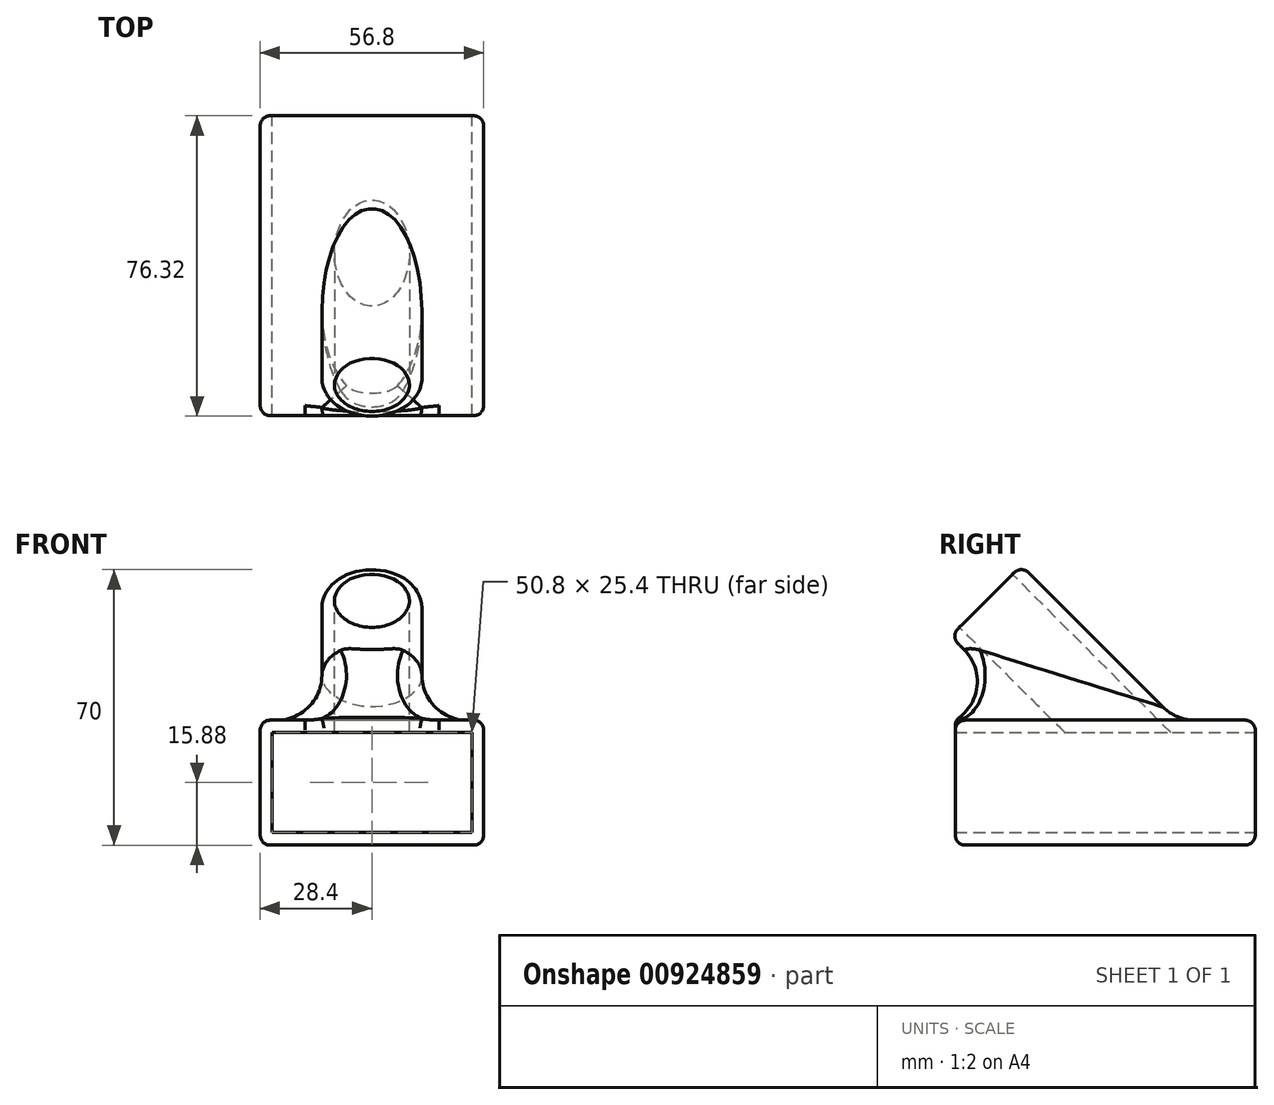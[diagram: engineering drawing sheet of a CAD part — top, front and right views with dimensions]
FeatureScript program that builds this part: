
annotation { "Feature Type Name" : "Feature", "Feature Type Description" : "" }
export const myFeature = defineFeature(function(context is Context, id is Id, definition is map)
    precondition{}
    {
        {
            var Q0;
            Q0=qCreatedBy(makeId("Front.planeOp"),FACE);
            var sketch = newSketch(context, id + "F0", { "sketchPlane" : qUnion([Q0])});
            skLineSegment(sketch, "E0.bottom", {"start": v(28.4, -15.88) * mm, "end": v(-28.4, -15.88) * mm});
            skLineSegment(sketch, "E0.top", {"start": v(28.4, 15.88) * mm, "end": v(-28.4, 15.87) * mm});
            skLineSegment(sketch, "E0.left", {"start": v(28.4, -15.88) * mm, "end": v(28.4, 15.88) * mm});
            skLineSegment(sketch, "E0.right", {"start": v(-28.4, -15.88) * mm, "end": v(-28.4, 15.88) * mm});
            skPoint(sketch, "E0.middle", {"position": v(0, 0) * mm});
            skLineSegment(sketch, "E1.bottom", {"start": v(25.4, -12.7) * mm, "end": v(-25.4, -12.7) * mm});
            skLineSegment(sketch, "E1.top", {"start": v(25.4, 12.7) * mm, "end": v(-25.4, 12.7) * mm});
            skLineSegment(sketch, "E1.left", {"start": v(25.4, -12.7) * mm, "end": v(25.4, 12.7) * mm});
            skLineSegment(sketch, "E1.right", {"start": v(-25.4, -12.7) * mm, "end": v(-25.4, 12.7) * mm});
            skSolve(sketch);
        }
        {
            var Q0;
            Q0 = qSketchRegion(id + "F0", true);
            extrude(context, id + "F1", {"entities" : qUnion([Q0]), "depth" : 38.1 * mm, "offsetDistance" : 25.4 * mm, "hasSecondDirection" : true, "secondDirectionOppositeDirection" : true, "secondDirectionDepth" : 38.1 * mm});
        }
        {
            var Q0;
            Q0=qCreatedBy(makeId("Front.planeOp"),FACE);
            var sketch = newSketch(context, id + "F2", { "sketchPlane" : qUnion([Q0])});
            skLineSegment(sketch, "E2", {"start": v(-74.55, 0) * mm, "end": v(74.23, 0) * mm});
            skSolve(sketch);
        }
        {
            var Q0;
            Q0=qCreatedBy(makeId("Front.planeOp"),FACE);
            var Q1;
            Q1=sQuery(id+"F2.wireOp",EDGE,"E2");
            cPlane(context, id + "F3", {"entities" : qUnion([Q0, Q1]), "cplaneType" : CPlaneType.LINE_ANGLE, "offset" : 25.4 * mm, "angle" : 45 * degree, "width" : 152.4 * mm, "height" : 152.4 * mm});
        }
        {
            var Q0;
            Q0=qCreatedBy(id+"F3.planeOp",FACE);
            var sketch = newSketch(context, id + "F4", { "sketchPlane" : qUnion([Q0])});
            skLineSegment(sketch, "E3", {"start": v(-88.35, 54.08) * mm, "end": v(88.37, 54.08) * mm});
            skSolve(sketch);
        }
        {
            var Q0;
            Q0=qCreatedBy(id+"F3.planeOp",FACE);
            var Q1;
            Q1=sQuery(id+"F4.wireOp",EDGE,"E3");
            cPlane(context, id + "F5", {"entities" : qUnion([Q0, Q1]), "cplaneType" : CPlaneType.LINE_ANGLE, "offset" : 25.4 * mm, "angle" : 90 * degree, "width" : 152.4 * mm, "height" : 152.4 * mm});
        }
        {
            var Q0;
            Q0=qCreatedBy(id+"F5.planeOp",FACE);
            var sketch = newSketch(context, id + "F6", { "sketchPlane" : qUnion([Q0])});
            skCircle(sketch, "E4", {"center": v(0, 11.25) * mm, "radius": 12.7 * mm});
            skCircle(sketch, "E5", {"center": v(0, 11.25) * mm, "radius": 9.53 * mm});
            skSolve(sketch);
        }
        {
            var Q0;
            Q0 = qSketchRegion(id + "F6", true);
            extrude(context, id + "F7", {"entities" : qUnion([Q0]), "operationType" : NewBodyOperationType.ADD, "oppositeDirection" : true, "depth" : 66.04 * mm, "offsetDistance" : 25.4 * mm});
        }
        {
            var Q0;
            Q0=makeQuery(id+"F7.boolean.opBoolean","INTERSECT",EDGE,{"derivedFrom":[makeQuery(id+"F1.opExtrude","SWEPT_FACE",FACE,{"disambiguationData":[OSD([sQuery(id+"F0.wireOp",EDGE,"E0.top")])]}),makeQuery(id+"F7.opExtrude","SWEPT_FACE",FACE,{"disambiguationData":[OSD([sQuery(id+"F6.wireOp",EDGE,"E4")])]})]});
            fillet(context, id + "F8", {"entities" : qUnion([Q0]), "radius" : 11.43 * mm, "tangentPropagation" : true, "allowEdgeOverflow" : false});
        }
        {
            var Q0;
            Q0=qCreatedBy(makeId("Front.planeOp"),FACE);
            var sketch = newSketch(context, id + "F9", { "sketchPlane" : qUnion([Q0])});
            skLineSegment(sketch, "E6.bottom", {"start": v(25.4, -12.7) * mm, "end": v(-25.4, -12.7) * mm});
            skLineSegment(sketch, "E6.top", {"start": v(25.4, 12.7) * mm, "end": v(-25.4, 12.7) * mm});
            skLineSegment(sketch, "E6.left", {"start": v(25.4, -12.7) * mm, "end": v(25.4, 12.7) * mm});
            skLineSegment(sketch, "E6.right", {"start": v(-25.4, -12.7) * mm, "end": v(-25.4, 12.7) * mm});
            skPoint(sketch, "E6.middle", {"position": v(0, 0) * mm});
            skSolve(sketch);
        }
        {
            var Q0;
            Q0 = qSketchRegion(id + "F9", true);
            extrude(context, id + "F10", {"entities" : qUnion([Q0]), "operationType" : NewBodyOperationType.REMOVE, "oppositeDirection" : true, "depth" : 25.4 * mm, "offsetDistance" : 25.4 * mm, "hasSecondDirection" : true, "secondDirectionOppositeDirection" : false, "secondDirectionDepth" : 25.4 * mm});
        }
        {
            var Q0;
            Q0=qCreatedBy(id+"F5.planeOp",FACE);
            var sketch = newSketch(context, id + "F11", { "sketchPlane" : qUnion([Q0])});
            skCircle(sketch, "E7", {"center": v(0, 11.25) * mm, "radius": 9.53 * mm});
            skSolve(sketch);
        }
        {
            var Q0;
            Q0 = qSketchRegion(id + "F11", true);
            extrude(context, id + "F12", {"entities" : qUnion([Q0]), "operationType" : NewBodyOperationType.REMOVE, "oppositeDirection" : true, "depth" : 65.8 * mm, "offsetDistance" : 25.4 * mm});
        }
        {
            var Q0;
            Q0=makeQuery(id+"F7.opExtrude","CAP_EDGE",EDGE,{"disambiguationData":[OSD([sQuery(id+"F6.wireOp",EDGE,"E4")])],"isStart":true});
            var Q1;
            Q1=makeQuery(id+"F1.opExtrude","SWEPT_EDGE",EDGE,{"disambiguationData":[OSD([sQuery(id+"F0.wireOp",EDGE,"E0.top"),sQuery(id+"F0.wireOp",EDGE,"E0.right")])]});
            var Q2;
            Q2=makeQuery(id+"F1.opExtrude","SWEPT_EDGE",EDGE,{"disambiguationData":[OSD([sQuery(id+"F0.wireOp",EDGE,"E0.top"),sQuery(id+"F0.wireOp",EDGE,"E0.left")])]});
            var Q3;
            Q3=makeQuery(id+"F1.opExtrude","SWEPT_EDGE",EDGE,{"disambiguationData":[OSD([sQuery(id+"F0.wireOp",EDGE,"E0.bottom"),sQuery(id+"F0.wireOp",EDGE,"E0.left")])]});
            var Q4;
            Q4=makeQuery(id+"F1.opExtrude","SWEPT_EDGE",EDGE,{"disambiguationData":[OSD([sQuery(id+"F0.wireOp",EDGE,"E0.bottom"),sQuery(id+"F0.wireOp",EDGE,"E0.right")])]});
            var Q5;
            Q5=makeQuery(id+"F1.opExtrude","CAP_EDGE",EDGE,{"disambiguationData":[OSD([sQuery(id+"F0.wireOp",EDGE,"E0.left")])],"isStart":true});
            var Q6;
            Q6=makeQuery(id+"F1.opExtrude","CAP_EDGE",EDGE,{"disambiguationData":[OSD([sQuery(id+"F0.wireOp",EDGE,"E0.bottom")])],"isStart":true});
            var Q7;
            Q7=makeQuery(id+"F1.opExtrude","CAP_EDGE",EDGE,{"disambiguationData":[OSD([sQuery(id+"F0.wireOp",EDGE,"E0.right")])],"isStart":true});
            var Q8;
            Q8=makeQuery(id+"F1.opExtrude","CAP_EDGE",EDGE,{"disambiguationData":[OSD([sQuery(id+"F0.wireOp",EDGE,"E0.top")])],"isStart":true});
            var Q9;
            Q9=makeQuery(id+"F1.opExtrude","CAP_EDGE",EDGE,{"disambiguationData":[OSD([sQuery(id+"F0.wireOp",EDGE,"E0.right")])],"isStart":false});
            var Q10;
            Q10=makeQuery(id+"F1.opExtrude","CAP_EDGE",EDGE,{"disambiguationData":[OSD([sQuery(id+"F0.wireOp",EDGE,"E0.bottom")])],"isStart":false});
            var Q11;
            Q11=makeQuery(id+"F1.opExtrude","CAP_EDGE",EDGE,{"disambiguationData":[OSD([sQuery(id+"F0.wireOp",EDGE,"E0.top")])],"isStart":false});
            var Q12;
            Q12=makeQuery(id+"F1.opExtrude","CAP_EDGE",EDGE,{"disambiguationData":[OSD([sQuery(id+"F0.wireOp",EDGE,"E0.left")])],"isStart":false});
            fillet(context, id + "F13", {"entities" : qUnion([Q0, Q1, Q2, Q3, Q4, Q5, Q6, Q7, Q8, Q9, Q10, Q11, Q12]), "radius" : 2.54 * mm, "tangentPropagation" : true, "allowEdgeOverflow" : false});
        }
    });
